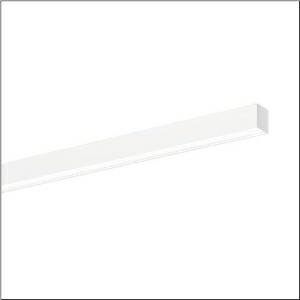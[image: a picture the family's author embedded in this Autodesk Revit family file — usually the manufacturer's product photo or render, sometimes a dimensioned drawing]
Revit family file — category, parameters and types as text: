
# Revit family: silica_21_51mx20da42wb
name_source: partatom
category: Lighting Fixtures
units: mm (PartAtom-declared; Revit-internal decimal feet)

## family parameters
Cut with Voids When Loaded = No
Host = Face
Light Source = No
Part Type = Normal
Room Calculation Point = No
Round Connector Dimension = Use Diameter
Shared = No

## types (1)
- --- (1 x LED, 2400 lm, 15.2 W, 4000K)
    Apparent Load = 15 VA
    CIE Flux Codes = 48 79 96 100 100
    Color Rendering = 80
    Color Temperature = 4000K
    Default Elevation = 1800 mm
    Description = Silica 21, office luminaire, primary optical cover: cover, of PMMA, opal, light emission: direct distribution, primary light characteristic: symmetric, installation type: surface-mounted, LED, rated luminous flux: 2.400lm, luminous efficacy: 158lm/W, light colour: 840, colour temperature: 4000K, control gear: DALI 2, with terminal, 3+2-pole, max. 2.5mm², mains connection: 220..240V, AC, 50/60Hz, rated input power: 15.2W, luminaire housing, of aluminium, traffic white (RAL 9016), length: 1.204mm, width: 53mm, height: 53mm, protection rating (complete): IP20, insulation class (complete): insulation class I (protective earthing), certification: CE, permissible operating ambient temperature: 0..+35°C, standard: EN 50419, packaging unit: 1 piece
    Height = 53 mm
    Lamp = 1 x LED
    Lamp Light Flux = 2400 lm
    Lamp Power = 15.2 W
    Lamp count = 1
    Length = 1204 mm
    Luminous efficacy = 158 lm/W
    Manufacturer = Siteco
    ModVariant = No
    Model = 51MX20DA42WB
    Mounting Place = Ceiling
    Mounting Type = Surface mounted
    Number of Poles = 1
    OnlyDefault = Yes
    Power Factor = 1
    Product Name = Silica 21
    Product group = office luminaire | ceiling mounted
    ProductGroupID = 301
    Protection Class = Protection class I
    Protection Degree = IP 20
    RLX_Detail_Level = 1
    RLX_Emergency_Light_Flux = 0 lm
    RLX_Emergency_Type = 0
    RLX_Emergency_Type_DB = No
    RlxData = <blob elided: 23885 chars, md5=f78a7c9c>
    Socket = socket
    Standby Power = 0 W
    System Light Flux = 2400 lm
    System Power = 15 W
    Type Comments = factory setting: luminous flux: 100 % | dim-lin: 254 | 218 mA
    Type Image = l_1335877.jpg
    URL = http://relux.com
    VarID = @adj_027953
    Voltage = 0 V
    Weight = 0.00 kg
    Width = 53 mm

## geometry (parser evidence)
native form markers: Blend x4, Sweep x9
no freeform markers — native parametric forms only
